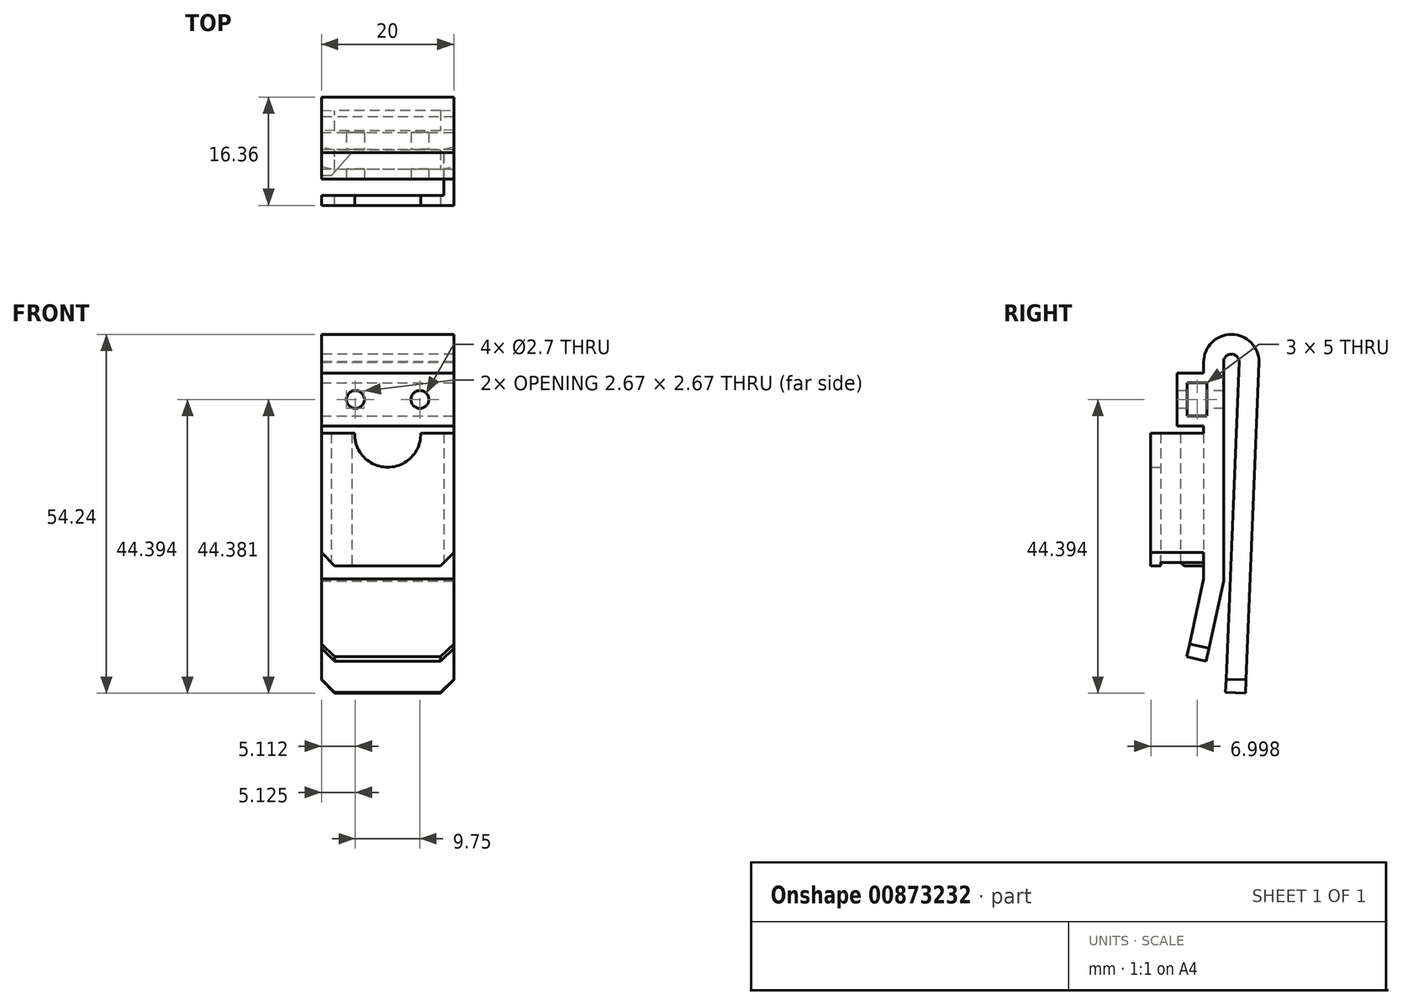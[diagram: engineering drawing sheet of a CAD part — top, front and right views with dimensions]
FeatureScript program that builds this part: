
annotation { "Feature Type Name" : "Feature", "Feature Type Description" : "" }
export const myFeature = defineFeature(function(context is Context, id is Id, definition is map)
    precondition{}
    {
        {
            var Q0;
            Q0=qCreatedBy(makeId("Right.planeOp"),FACE);
            var sketch = newSketch(context, id + "F0", { "sketchPlane" : qUnion([Q0])});
            skLineSegment(sketch, "E0", {"start": v(-3.3, 16.7) * mm, "end": v(-3.3, -16.26) * mm});
            skLineSegment(sketch, "E1", {"start": v(2.06, 16.7) * mm, "end": v(0, -33.3) * mm});
            skArc(sketch, "E2", {"start": v(-3.3, 16.7) * mm, "mid": v(-0.62, 19.38) * mm, "end": v(2.06, 16.7) * mm});
            skLineSegment(sketch, "E3", {"start": v(-3.3, -16.26) * mm, "end": v(-5.9, -28.2) * mm});
            skSolve(sketch);
        }
        {
            var Q0;
            Q0=qCreatedBy(makeId("Top.planeOp"),FACE);
            var sketch = newSketch(context, id + "F1", { "sketchPlane" : qUnion([Q0])});
            skLineSegment(sketch, "E4.bottom", {"start": v(10, -1.8) * mm, "end": v(-10, -1.8) * mm});
            skLineSegment(sketch, "E4.top", {"start": v(10, -4.8) * mm, "end": v(-10, -4.8) * mm});
            skLineSegment(sketch, "E4.left", {"start": v(10, -1.8) * mm, "end": v(10, -4.8) * mm});
            skLineSegment(sketch, "E4.right", {"start": v(-10, -1.8) * mm, "end": v(-10, -4.8) * mm});
            skLineSegment(sketch, "E5", {"start": v(10, -1.8) * mm, "end": v(-10, -4.8) * mm, "construction": true});
            skPoint(sketch, "E6", {"position": v(0, -3.3) * mm});
            skSolve(sketch);
        }
        {
            var Q0;
            Q0=makeQuery(id+"F1.imprint","IMPRINT",FACE,{"disambiguationData":[TD([[makeQuery(id+"F1.imprint","IMPRINT",EDGE,{"derivedFrom":sQuery(id+"F1.wireOp",EDGE,"E4.bottom")}),1.0]])]});
            var Q1;
            Q1 = qConstructionFilter(qBodyType(qCreatedBy(id + "F0" ,EDGE), BodyType.WIRE), ConstructionObject.NO);
            sweep(context, id + "F2", {"profiles" : qUnion([Q0]), "path" : qUnion([Q1])});
        }
        {
            var Q0;
            Q0=makeQuery(id+"F2.opSweep","CAP_EDGE",EDGE,{"disambiguationData":[OSD([sQuery(id+"F0.wireOp",VERTEX,"XrpDJy1t-CrfH-aBQF-mr9F-7XAcLQNUa5PQ.end"),sQuery(id+"F1.wireOp",EDGE,"E4.right")])],"isStart":false});
            var Q1;
            Q1=makeQuery(id+"F2.opSweep","CAP_EDGE",EDGE,{"disambiguationData":[OSD([sQuery(id+"F0.wireOp",VERTEX,"XrpDJy1t-CrfH-aBQF-mr9F-7XAcLQNUa5PQ.end"),sQuery(id+"F1.wireOp",EDGE,"E4.left")])],"isStart":false});
            var Q2;
            Q2=makeQuery(id+"F2.opSweep","CAP_EDGE",EDGE,{"disambiguationData":[OSD([sQuery(id+"F0.wireOp",VERTEX,"E0.end"),sQuery(id+"F1.wireOp",EDGE,"E4.right")])],"isStart":true});
            var Q3;
            Q3=makeQuery(id+"F2.opSweep","CAP_EDGE",EDGE,{"disambiguationData":[OSD([sQuery(id+"F0.wireOp",VERTEX,"E0.end"),sQuery(id+"F1.wireOp",EDGE,"E4.left")])],"isStart":true});
            chamfer(context, id + "F3", {"entities" : qUnion([Q0, Q1, Q2, Q3]), "width" : 2 * mm, "tangentPropagation" : true});
        }
        {
            var Q0;
            Q0=makeQuery(id+"F2.opSweep","SWEPT_FACE",FACE,{"disambiguationData":[OSD([sQuery(id+"F0.wireOp",EDGE,"E0"),sQuery(id+"F1.wireOp",EDGE,"E4.top")])]});
            var sketch = newSketch(context, id + "F4", { "sketchPlane" : qUnion([Q0])});
            skLineSegment(sketch, "E7.bottom", {"start": v(-5.13, 13.28) * mm, "end": v(5.12, 13.28) * mm, "construction": true});
            skLineSegment(sketch, "E7.top", {"start": v(-5.13, -12.32) * mm, "end": v(5.12, -12.32) * mm, "construction": true});
            skLineSegment(sketch, "E7.left", {"start": v(-7.13, 11.28) * mm, "end": v(-7.13, -10.32) * mm, "construction": true});
            skLineSegment(sketch, "E7.right", {"start": v(7.12, 11.28) * mm, "end": v(7.12, -10.32) * mm, "construction": true});
            skPoint(sketch, "E8", {"position": v(0, 0) * mm});
            skCircle(sketch, "E9", {"center": v(-4.88, 11.03) * mm, "radius": 1.35 * mm});
            skPoint(sketch, "E10.visualSharp", {"position": v(-7.13, 13.28) * mm});
            skArc(sketch, "E10.filletArc", {"start": v(-5.13, 13.28) * mm, "mid": v(-6.54, 12.7) * mm, "end": v(-7.13, 11.28) * mm, "construction": true});
            skPoint(sketch, "E11.visualSharp", {"position": v(7.12, 13.28) * mm});
            skArc(sketch, "E11.filletArc", {"start": v(7.12, 11.28) * mm, "mid": v(6.54, 12.7) * mm, "end": v(5.12, 13.28) * mm, "construction": true});
            skPoint(sketch, "E12.visualSharp", {"position": v(7.12, -12.32) * mm});
            skArc(sketch, "E12.filletArc", {"start": v(5.12, -12.32) * mm, "mid": v(6.54, -11.73) * mm, "end": v(7.12, -10.32) * mm, "construction": true});
            skPoint(sketch, "E13.visualSharp", {"position": v(-7.13, -12.32) * mm});
            skArc(sketch, "E13.filletArc", {"start": v(-7.13, -10.32) * mm, "mid": v(-6.54, -11.73) * mm, "end": v(-5.13, -12.32) * mm, "construction": true});
            skCircle(sketch, "E14.1.0.0", {"center": v(4.87, 11.03) * mm, "radius": 1.35 * mm});
            skLineSegment(sketch, "E14.direction1", {"start": v(-4.88, 11.03) * mm, "end": v(4.87, 11.03) * mm, "construction": true});
            skLineSegment(sketch, "E15.bottom", {"start": v(-10, 5.94) * mm, "end": v(-5, 5.94) * mm});
            skLineSegment(sketch, "E15.top", {"start": v(-10, -14.1) * mm, "end": v(10, -14.1) * mm});
            skLineSegment(sketch, "E15.left", {"start": v(-10, 5.94) * mm, "end": v(-10, -14.1) * mm});
            skLineSegment(sketch, "E15.right", {"start": v(10, 5.94) * mm, "end": v(10, -14.1) * mm});
            skLineSegment(sketch, "E16", {"start": v(-10, 5.94) * mm, "end": v(10, -14.1) * mm, "construction": true});
            skPoint(sketch, "E17", {"position": v(0, -4.08) * mm});
            skLineSegment(sketch, "E18", {"start": v(-5, 5.94) * mm, "end": v(5, 5.94) * mm});
            skLineSegment(sketch, "E19", {"start": v(5, 5.94) * mm, "end": v(10, 5.94) * mm});
            skArc(sketch, "E20", {"start": v(5, 5.94) * mm, "mid": v(0, 10.78) * mm, "end": v(-5, 5.94) * mm, "construction": true});
            skArc(sketch, "E21", {"start": v(-5, 5.94) * mm, "mid": v(0, 0.78) * mm, "end": v(5, 5.94) * mm});
            skLineSegment(sketch, "E22.bottom", {"start": v(-10, 15.03) * mm, "end": v(10, 15.03) * mm});
            skLineSegment(sketch, "E22.top", {"start": v(-10, 7.03) * mm, "end": v(10, 7.03) * mm});
            skLineSegment(sketch, "E22.left", {"start": v(-10, 15.03) * mm, "end": v(-10, 7.03) * mm});
            skLineSegment(sketch, "E22.right", {"start": v(10, 15.03) * mm, "end": v(10, 7.03) * mm});
            skSolve(sketch);
        }
        {
            var Q0;
            Q0=makeQuery(id+"F4.imprint","IMPRINT",FACE,{"disambiguationData":[TD([[makeQuery(id+"F4.imprint","IMPRINT",EDGE,{"derivedFrom":sQuery(id+"F4.wireOp",EDGE,"E9")}),1.0]])]});
            var Q1;
            Q1=makeQuery(id+"F4.imprint","IMPRINT",FACE,{"disambiguationData":[TD([[makeQuery(id+"F4.imprint","IMPRINT",EDGE,{"derivedFrom":sQuery(id+"F4.wireOp",EDGE,"E14.1.0.0")}),1.0]])]});
            extrude(context, id + "F5", {"entities" : qUnion([Q0, Q1]), "operationType" : NewBodyOperationType.REMOVE, "endBound" : BoundingType.UP_TO_NEXT, "oppositeDirection" : true, "depth" : 25 * mm, "offsetDistance" : 25 * mm});
        }
        {
            var Q0;
            Q0=makeQuery(id+"F4.imprint","IMPRINT",FACE,{"disambiguationData":[TD([[makeQuery(id+"F4.imprint","IMPRINT",EDGE,{"derivedFrom":sQuery(id+"F4.wireOp",EDGE,"E9")}),-1.0]])]});
            var Q1;
            Q1=makeQuery(id+"F4.imprint","IMPRINT",FACE,{"disambiguationData":[TD([[makeQuery(id+"F4.imprint","IMPRINT",EDGE,{"derivedFrom":sQuery(id+"F4.wireOp",EDGE,"E14.1.0.0")}),-1.0]])]});
            extrude(context, id + "F6", {"entities" : qUnion([Q0, Q1]), "operationType" : NewBodyOperationType.ADD, "depth" : 4 * mm, "offsetDistance" : 25 * mm});
        }
        {
            var Q0;
            Q0=makeQuery(id+"F4.imprint","IMPRINT",FACE,{"disambiguationData":[TD([[makeQuery(id+"F4.imprint","IMPRINT",EDGE,{"derivedFrom":sQuery(id+"F4.wireOp",EDGE,"E15.bottom")}),-1.0]])]});
            extrude(context, id + "F7", {"entities" : qUnion([Q0]), "operationType" : NewBodyOperationType.ADD, "depth" : 8 * mm, "offsetDistance" : 25 * mm});
        }
        {
            var Q0;
            Q0=makeQuery(id+"F7.opExtrude","SWEPT_FACE",FACE,{"disambiguationData":[OSD([sQuery(id+"F4.wireOp",EDGE,"E15.top")])]});
            var sketch = newSketch(context, id + "F8", { "sketchPlane" : qUnion([Q0])});
            skLineSegment(sketch, "E23.bottom", {"start": v(-8.5, 11.3) * mm, "end": v(8.5, 11.3) * mm});
            skLineSegment(sketch, "E23.top", {"start": v(-5.4, 4.8) * mm, "end": v(8.5, 4.8) * mm});
            skLineSegment(sketch, "E23.left", {"start": v(-8.5, 4.8) * mm, "end": v(-8.5, 4.8) * mm});
            skLineSegment(sketch, "E23.right", {"start": v(8.5, 4.8) * mm, "end": v(8.5, 4.8) * mm});
            skLineSegment(sketch, "E24", {"start": v(-8.5, 11.3) * mm, "end": v(8.5, 4.8) * mm, "construction": true});
            skPoint(sketch, "E25", {"position": v(0, 8.05) * mm});
            skPoint(sketch, "E26.visualSharp", {"position": v(-8.5, 11.3) * mm});
            skPoint(sketch, "E27.visualSharp", {"position": v(8.5, 11.3) * mm});
            skLineSegment(sketch, "E28", {"start": v(-8.5, 8.3) * mm, "end": v(-8.5, 11.3) * mm});
            skLineSegment(sketch, "E29", {"start": v(8.5, 11.3) * mm, "end": v(8.5, 4.8) * mm});
            skPoint(sketch, "E30", {"position": v(0, 11.3) * mm});
            skPoint(sketch, "E31", {"position": v(-8.5, 8.3) * mm});
            skLineSegment(sketch, "E32", {"start": v(-8.5, 8.3) * mm, "end": v(-5.4, 4.8) * mm});
            skSolve(sketch);
        }
        {
            var Q0;
            Q0=makeQuery(id+"F8.imprint","IMPRINT",FACE,{"disambiguationData":[TD([[makeQuery(id+"F8.imprint","IMPRINT",EDGE,{"derivedFrom":sQuery(id+"F8.wireOp",EDGE,"E23.bottom")}),-1.0]])]});
            extrude(context, id + "F9", {"entities" : qUnion([Q0]), "operationType" : NewBodyOperationType.REMOVE, "endBound" : BoundingType.UP_TO_NEXT, "oppositeDirection" : true, "depth" : 25 * mm, "offsetDistance" : 25 * mm});
        }
        {
            var Q0;
            Q0=makeQuery(id+"F7.boolean.opBoolean","MERGE",FACE,{"derivedFrom":[makeQuery(id+"F6.boolean.opBoolean","MERGE",FACE,{"derivedFrom":[makeQuery(id+"F2.opSweep","SWEPT_FACE",FACE,{"disambiguationData":[OSD([sQuery(id+"F0.wireOp",EDGE,"E3"),sQuery(id+"F1.wireOp",EDGE,"E4.right")])]}),makeQuery(id+"F6.opExtrude","SWEPT_FACE",FACE,{"disambiguationData":[OSD([sQuery(id+"F4.wireOp",EDGE,"E22.left")])]})]}),makeQuery(id+"F7.opExtrude","SWEPT_FACE",FACE,{"disambiguationData":[OSD([sQuery(id+"F4.wireOp",EDGE,"E15.left")])]})]});
            var sketch = newSketch(context, id + "F10", { "sketchPlane" : qUnion([Q0])});
            skLineSegment(sketch, "E33.bottom", {"start": v(4.8, 5.94) * mm, "end": v(11.3, 5.94) * mm});
            skLineSegment(sketch, "E33.top", {"start": v(8.3, -14.1) * mm, "end": v(11.3, -14.1) * mm});
            skLineSegment(sketch, "E33.left", {"start": v(8.3, 5.94) * mm, "end": v(8.3, -14.1) * mm});
            skLineSegment(sketch, "E33.right", {"start": v(11.3, 5.94) * mm, "end": v(11.3, -14.1) * mm});
            skLineSegment(sketch, "E34.0.0", {"start": v(4.8, -14.1) * mm, "end": v(11.3, -14.1) * mm});
            skLineSegment(sketch, "E34.0.2", {"start": v(11.3, -14.1) * mm, "end": v(8.3, -14.1) * mm});
            skLineSegment(sketch, "E35", {"start": v(4.8, -14.1) * mm, "end": v(12.8, -14.1) * mm});
            skSolve(sketch);
        }
        {
            var Q0;
            Q0=makeQuery(id+"F10.imprint","IMPRINT",FACE,{"disambiguationData":[TD([[makeQuery(id+"F10.imprint","IMPRINT",EDGE,{"derivedFrom":sQuery(id+"F10.wireOp",EDGE,"E33.bottom")}),1.0]])]});
            extrude(context, id + "F11", {"entities" : qUnion([Q0]), "operationType" : NewBodyOperationType.REMOVE, "endBound" : BoundingType.UP_TO_NEXT, "oppositeDirection" : true, "depth" : 25 * mm, "offsetDistance" : 25 * mm});
        }
        {
            var Q0;
            Q0=makeQuery(id+"F7.opExtrude","SWEPT_EDGE",EDGE,{"disambiguationData":[OSD([sQuery(id+"F0.wireOp",EDGE,"E0"),sQuery(id+"F1.wireOp",EDGE,"E4.top"),sQuery(id+"F1.wireOp",EDGE,"E4.left"),sQuery(id+"F4.wireOp",EDGE,"E15.top"),sQuery(id+"F4.wireOp",EDGE,"E15.right")])]});
            var Q1;
            Q1=makeQuery(id+"F7.opExtrude","SWEPT_EDGE",EDGE,{"disambiguationData":[OSD([sQuery(id+"F0.wireOp",EDGE,"E0"),sQuery(id+"F1.wireOp",EDGE,"E4.top"),sQuery(id+"F1.wireOp",EDGE,"E4.right"),sQuery(id+"F4.wireOp",EDGE,"E15.top"),sQuery(id+"F4.wireOp",EDGE,"E15.left")])]});
            chamfer(context, id + "F12", {"entities" : qUnion([Q0, Q1]), "width" : 2 * mm, "tangentPropagation" : true});
        }
        {
            var Q0;
            Q0=qCreatedBy(makeId("Right.planeOp"),FACE);
            var sketch = newSketch(context, id + "F13", { "sketchPlane" : qUnion([Q0])});
            skPoint(sketch, "E36.oppositeSnap0", {"position": v(-4.3, 8.03) * mm});
            skLineSegment(sketch, "E36.bottom", {"start": v(-4.3, 13.53) * mm, "end": v(-7.3, 13.53) * mm});
            skLineSegment(sketch, "E36.top", {"start": v(-7.3, 8.53) * mm, "end": v(-4.3, 8.53) * mm});
            skLineSegment(sketch, "E36.left", {"start": v(-7.3, 13.53) * mm, "end": v(-7.3, 8.53) * mm});
            skLineSegment(sketch, "E36.right", {"start": v(-4.3, 13.53) * mm, "end": v(-4.3, 8.53) * mm});
            skLineSegment(sketch, "E37.0", {"start": v(-8.8, 15.03) * mm, "end": v(-4.8, 15.03) * mm, "construction": true});
            skLineSegment(sketch, "E38.0", {"start": v(-8.8, 7.03) * mm, "end": v(-4.8, 7.03) * mm, "construction": true});
            skLineSegment(sketch, "E39.0", {"start": v(-8.8, 7.03) * mm, "end": v(-8.8, 15.03) * mm});
            skLineSegment(sketch, "E40", {"start": v(-6.8, 7.03) * mm, "end": v(-6.8, 8.53) * mm, "construction": true});
            skPoint(sketch, "E40.endSnap0", {"position": v(-6.8, 7.03) * mm});
            skLineSegment(sketch, "E41", {"start": v(-6.8, 15.03) * mm, "end": v(-6.8, 13.53) * mm, "construction": true});
            skPoint(sketch, "E41.endSnap0", {"position": v(-5.8, 13.53) * mm});
            skSolve(sketch);
        }
        {
            var Q0;
            Q0 = qSketchRegion(id + "F13", true);
            var Q1;
            Q1=sQuery(id+"F13.wireOp",EDGE,"E36.right");
            extrude(context, id + "F14", {"entities" : qUnion([Q0]), "operationType" : NewBodyOperationType.REMOVE, "surfaceEntities" : qUnion([Q1]), "endBound" : BoundingType.SYMMETRIC, "oppositeDirection" : true, "depth" : 25 * mm, "offsetDistance" : 25 * mm});
        }
    });
